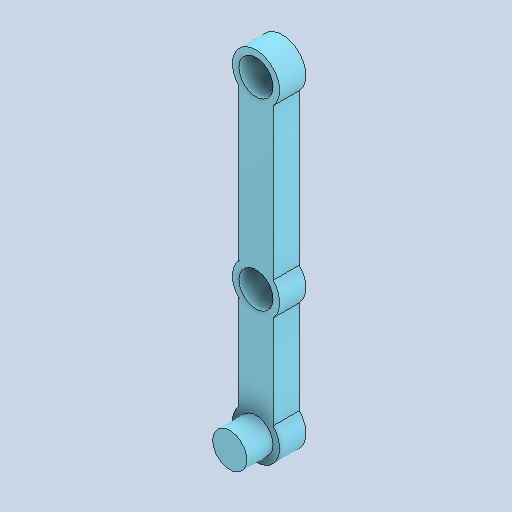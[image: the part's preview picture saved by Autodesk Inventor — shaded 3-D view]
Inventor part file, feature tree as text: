
AUTODESK INVENTOR PART (.ipt)
format: ipt  version: 2022 (Build 260153000, 153)  size: 125,440 bytes
history: native  units: in
note: dims shown in document units (in); Inventor stores cm internally (conversion verified against a paired STEP export)
features: other x3, sketch x1
ambient origin geometry x8: Origin, YZ Plane, XZ Plane, XY Plane, X Axis, Y Axis, Z Axis, Center Point
bodies: Solid1 (feature_tree)
feature tree (4):
  other  "Component27.ipt"
  other  "Solid1::Component27.ipt"
  other  "TaggingFeature1"
  sketch  "Sketch2"  dims[d0=0.3937in]
